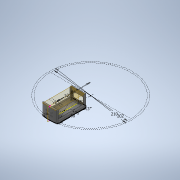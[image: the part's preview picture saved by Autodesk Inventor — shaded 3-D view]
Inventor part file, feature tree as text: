
AUTODESK INVENTOR PART (.ipt)
format: ipt  version: 2020 (Build 240168000, 168)  size: 345,088 bytes
history: native  units: mm
features: projected_geometry x22, extrude x9, sketch x8, other x5
ambient origin geometry x8: Origin, YZ Plane, XZ Plane, XY Plane, X Axis, Y Axis, Z Axis, Center Point
bodies: Body1 (feature_tree)
feature tree (44):
  other  "Твердое тело1"
  sketch  "Эскиз1"
  extrude  "Выдавливание3"  Depth=202.0mm
  other  "РабПлоскость1"
  extrude  "Выдавливание1"  Depth=35.0mm
  other  "РабПлоскость2"
  sketch  "Эскиз2"
  extrude  "Выдавливание4"  Depth=68.0mm
  extrude  "Выдавливание5"  Depth=2.0mm
  sketch  "Эскиз4"
  extrude  "Выдавливание6"  Depth=2.0mm
  extrude  "Выдавливание7"  Depth=3.0mm
  other  "РабПлоскость3"
  extrude  "Выдавливание8"  Depth=3.0mm
  other  "РабПлоскость4"
  extrude  "Выдавливание9"  Depth=210.0mm
  extrude  "Выдавливание10"  Depth=20.0mm TaperAngle=0.0deg
  projected_geometry  "Спроецированная петля1"
  projected_geometry  "Спроецированная петля7"
  projected_geometry  "Спроецированная петля8"
  sketch  "Эскиз3"
  projected_geometry  "Спроецированная петля9"
  projected_geometry  "Спроецированная петля10"
  projected_geometry  "Спроецированная петля11"
  projected_geometry  "Спроецированная петля12"
  sketch  "Эскиз5"
  projected_geometry  "Спроецированная петля13"
  projected_geometry  "Спроецированная петля14"
  projected_geometry  "Спроецированная петля15"
  projected_geometry  "Спроецированная петля16"
  projected_geometry  "Спроецированная петля17"
  sketch  "Эскиз6"
  sketch  "Эскиз7"
  projected_geometry  "Спроецированная петля18"
  projected_geometry  "Спроецированная петля19"
  projected_geometry  "Спроецированная петля20"
  projected_geometry  "Спроецированная петля21"
  projected_geometry  "Спроецированная петля22"
  projected_geometry  "Спроецированная петля23"
  projected_geometry  "Спроецированная петля24"
  sketch  "Эскиз8"
  projected_geometry  "Спроецированная петля25"
  projected_geometry  "Спроецированная петля26"
  projected_geometry  "Спроецированная петля27"
